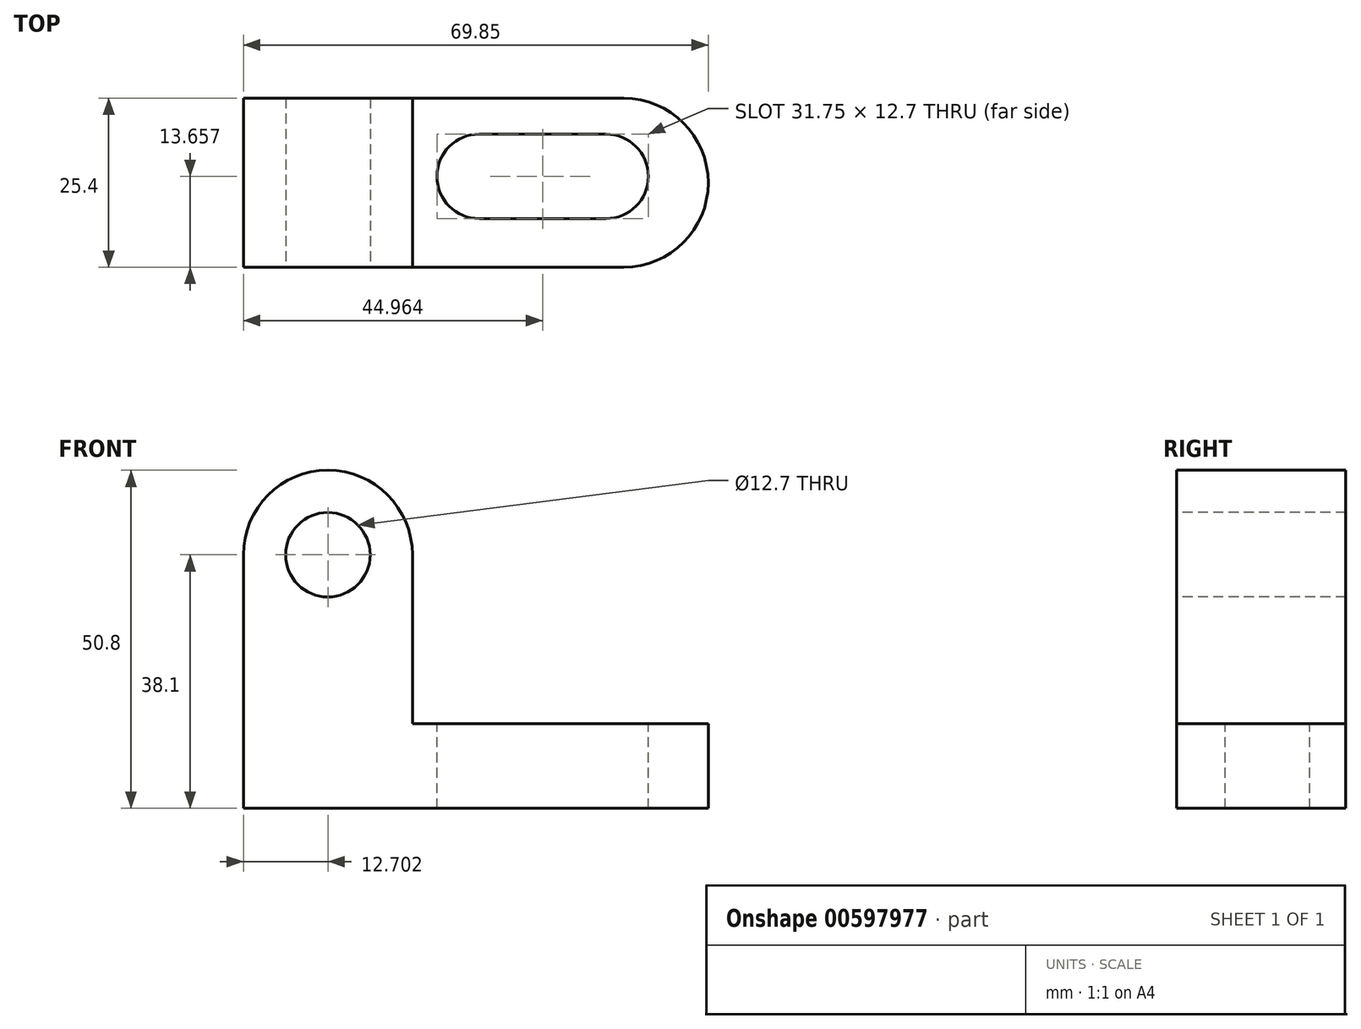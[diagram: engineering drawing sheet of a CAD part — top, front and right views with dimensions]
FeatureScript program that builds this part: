
annotation { "Feature Type Name" : "Feature", "Feature Type Description" : "" }
export const myFeature = defineFeature(function(context is Context, id is Id, definition is map)
    precondition{}
    {
        {
            var Q0;
            Q0=qCreatedBy(makeId("Front.planeOp"),FACE);
            var sketch = newSketch(context, id + "F0", { "sketchPlane" : qUnion([Q0])});
            skLineSegment(sketch, "E0", {"start": v(-47.54, 0) * mm, "end": v(22.31, 0) * mm});
            skLineSegment(sketch, "E1", {"start": v(22.31, 0) * mm, "end": v(22.31, 12.7) * mm});
            skLineSegment(sketch, "E2", {"start": v(22.31, 12.7) * mm, "end": v(-22.14, 12.7) * mm});
            skLineSegment(sketch, "E3", {"start": v(-22.14, 12.7) * mm, "end": v(-22.14, 38.1) * mm});
            skLineSegment(sketch, "E4", {"start": v(-47.54, 0) * mm, "end": v(-47.54, 38.1) * mm});
            skArc(sketch, "E5", {"start": v(-22.14, 38.1) * mm, "mid": v(-34.84, 50.8) * mm, "end": v(-47.54, 38.1) * mm});
            skSolve(sketch);
        }
        {
            var Q0;
            Q0=makeQuery(id+"F0.imprint","IMPRINT",FACE,{"disambiguationData":[TD([[makeQuery(id+"F0.imprint","IMPRINT",EDGE,{"derivedFrom":sQuery(id+"F0.wireOp",EDGE,"E0")}),1.0]])]});
            extrude(context, id + "F1", {"entities" : qUnion([Q0]), "depth" : 25.4 * mm, "offsetDistance" : 25.4 * mm});
        }
        {
            var Q0;
            Q0=makeQuery(id+"F1.opExtrude","CAP_FACE",FACE,{"disambiguationData":[OSD([sQuery(id+"F0.wireOp",EDGE,"E0"),sQuery(id+"F0.wireOp",EDGE,"E1"),sQuery(id+"F0.wireOp",EDGE,"E2"),sQuery(id+"F0.wireOp",EDGE,"E3"),sQuery(id+"F0.wireOp",EDGE,"E4"),sQuery(id+"F0.wireOp",EDGE,"E5")])],"isStart":false});
            var sketch = newSketch(context, id + "F2", { "sketchPlane" : qUnion([Q0])});
            skCircle(sketch, "E6", {"center": v(-34.84, 38.1) * mm, "radius": 6.35 * mm});
            skSolve(sketch);
        }
        {
            var Q0;
            Q0=makeQuery(id+"F2.imprint","IMPRINT",FACE,{"disambiguationData":[TD([[makeQuery(id+"F2.imprint","IMPRINT",EDGE,{"derivedFrom":sQuery(id+"F2.wireOp",EDGE,"E6")}),1.0]])]});
            extrude(context, id + "F3", {"entities" : qUnion([Q0]), "operationType" : NewBodyOperationType.REMOVE, "oppositeDirection" : true, "depth" : 25.4 * mm, "offsetDistance" : 25.4 * mm});
        }
        {
            var Q0;
            Q0=makeQuery(id+"F1.opExtrude","SWEPT_FACE",FACE,{"disambiguationData":[OSD([sQuery(id+"F0.wireOp",EDGE,"E2")])]});
            var sketch = newSketch(context, id + "F4", { "sketchPlane" : qUnion([Q0])});
            skArc(sketch, "E7", {"start": v(9.61, -25.4) * mm, "mid": v(22.31, -12.7) * mm, "end": v(9.61, 0) * mm});
            skSolve(sketch);
        }
        {
            var Q0;
            {var subQ0=sQuery(id+"F4.wireOp",EDGE,"E7");var subQ1=sQuery(id+"F0.wireOp",EDGE,"E2");var subQ2=makeQuery(id+"F1.opExtrude","CAP_EDGE",EDGE,{"disambiguationData":[OSD([subQ1])],"isStart":true});var subQ3=makeQuery(id+"F4.imprint","INTERSECT",VERTEX,{"derivedFrom":[subQ2,subQ0]});Q0=makeQuery(id+"F4.imprint","IMPRINT",FACE,{"disambiguationData":[TD([[makeQuery(id+"F4.imprint","IMPRINT",EDGE,{"disambiguationData":[TD([[subQ3,1.0]])],"derivedFrom":subQ0}),-1.0]])]});}
            var Q1;
            {var subQ0=sQuery(id+"F4.wireOp",EDGE,"E7");var subQ1=sQuery(id+"F0.wireOp",EDGE,"E2");var subQ2=makeQuery(id+"F1.opExtrude","CAP_EDGE",EDGE,{"disambiguationData":[OSD([subQ1])],"isStart":false});var subQ3=makeQuery(id+"F4.imprint","INTERSECT",VERTEX,{"derivedFrom":[subQ2,subQ0]});Q1=makeQuery(id+"F4.imprint","IMPRINT",FACE,{"disambiguationData":[TD([[makeQuery(id+"F4.imprint","IMPRINT",EDGE,{"disambiguationData":[TD([[subQ3,-1.0]])],"derivedFrom":subQ0}),-1.0]])]});}
            extrude(context, id + "F5", {"entities" : qUnion([Q0, Q1]), "operationType" : NewBodyOperationType.REMOVE, "oppositeDirection" : true, "depth" : 25.4 * mm, "offsetDistance" : 25.4 * mm});
        }
        {
            var Q0;
            Q0=makeQuery(id+"F1.opExtrude","SWEPT_FACE",FACE,{"disambiguationData":[OSD([sQuery(id+"F0.wireOp",EDGE,"E2")])]});
            var sketch = newSketch(context, id + "F6", { "sketchPlane" : qUnion([Q0])});
            skCircle(sketch, "E8", {"center": v(-12.1, -11.74) * mm, "radius": 6.35 * mm});
            skCircle(sketch, "E9", {"center": v(6.95, -11.74) * mm, "radius": 6.35 * mm});
            skLineSegment(sketch, "E10", {"start": v(-12.1, -5.4) * mm, "end": v(6.95, -5.4) * mm});
            skLineSegment(sketch, "E11", {"start": v(6.95, -5.4) * mm, "end": v(6.95, -18.1) * mm});
            skLineSegment(sketch, "E12", {"start": v(6.95, -18.1) * mm, "end": v(-12.1, -18.1) * mm});
            skLineSegment(sketch, "E13", {"start": v(-12.1, -18.1) * mm, "end": v(-12.1, -5.4) * mm});
            skSolve(sketch);
        }
        {
            var Q0;
            {var subQ0=sQuery(id+"F6.wireOp",EDGE,"E13");Q0=makeQuery(id+"F6.imprint","IMPRINT",FACE,{"disambiguationData":[TD([[makeQuery(id+"F6.imprint","IMPRINT",EDGE,{"derivedFrom":subQ0}),-1.0]])]});}
            var Q1;
            {var subQ0=sQuery(id+"F6.wireOp",EDGE,"E13");Q1=makeQuery(id+"F6.imprint","IMPRINT",FACE,{"disambiguationData":[TD([[makeQuery(id+"F6.imprint","IMPRINT",EDGE,{"derivedFrom":subQ0}),1.0]])]});}
            var Q2;
            {var subQ1=sQuery(id+"F6.wireOp",EDGE,"E10");Q2=makeQuery(id+"F6.imprint","IMPRINT",FACE,{"disambiguationData":[TD([[makeQuery(id+"F6.imprint","IMPRINT",EDGE,{"derivedFrom":subQ1}),-1.0]])]});}
            var Q3;
            {var subQ0=sQuery(id+"F6.wireOp",EDGE,"E11");Q3=makeQuery(id+"F6.imprint","IMPRINT",FACE,{"disambiguationData":[TD([[makeQuery(id+"F6.imprint","IMPRINT",EDGE,{"derivedFrom":subQ0}),-1.0]])]});}
            var Q4;
            {var subQ0=sQuery(id+"F6.wireOp",EDGE,"E11");Q4=makeQuery(id+"F6.imprint","IMPRINT",FACE,{"disambiguationData":[TD([[makeQuery(id+"F6.imprint","IMPRINT",EDGE,{"derivedFrom":subQ0}),1.0]])]});}
            extrude(context, id + "F7", {"entities" : qUnion([Q0, Q1, Q2, Q3, Q4]), "operationType" : NewBodyOperationType.REMOVE, "endBound" : BoundingType.THROUGH_ALL, "oppositeDirection" : true, "depth" : 25.4 * mm, "offsetDistance" : 25.4 * mm});
        }
    });
